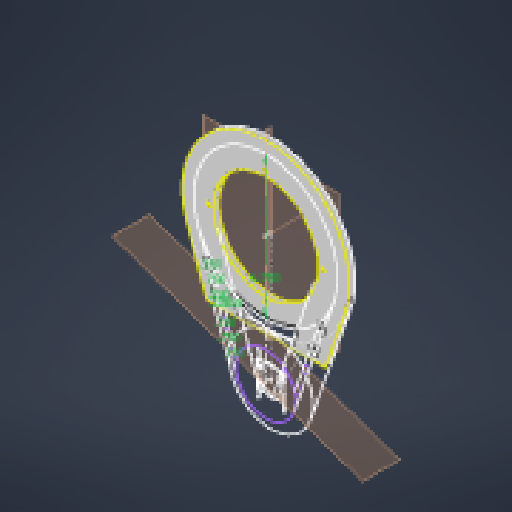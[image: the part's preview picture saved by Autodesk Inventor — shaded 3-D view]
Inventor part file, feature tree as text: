
AUTODESK INVENTOR PART (.ipt)
format: ipt  version: 2024 (Build 280153000, 153)  size: 336,384 bytes
history: native  units: in
note: dims shown in document units (in); Inventor stores cm internally (conversion verified against a paired STEP export)
features: other x7, plane x3, sketch x3, extrude x3, fillet x2, reference x2, mirror x1, hole x1, projected_geometry x1
ambient origin geometry x8: Origin, YZ Plane, XZ Plane, XY Plane, X Axis, Y Axis, Z Axis, Center Point
bodies: Solid1 (feature_tree)
feature tree (23):
  plane  "Work Plane1"
  sketch  "Sketch1"  dims[d0=0.9518in d1=6.0in]
  extrude  "Extrusion1"  Depth=6.0in
  sketch  "Sketch2"  dims[d2=0.25in d3=0.0in d4=7.874in d5=3.937in d6=1.22in]
  extrude  "Extrusion2"  Depth=3.937in
  fillet  "Fillet1"  Radius=3.937in
  fillet  "Fillet2"  Radius=1.22in
  plane  "Work Plane2"
  extrude  "Extrusion3"  Depth=0.35in
  plane  "Work Plane3"
  mirror  "Mirror1"
  hole  "Hole1"  [1 undecoded]
  reference  "Reference1"
  reference  "Reference3"
  projected_geometry  "Projected Loop1"
  sketch  "Sketch3"  dims[d7=1.22in d8=0.134in d9=0.75in d10=0.248in d11=0.25in d12=90.0deg d13=1.0in d14=0.8108in d15=0.35in d16=0.1181in d17=0.35in d18=0.1181in d19=0.35in d20=0.1181in d21=0.35in d22=0.1181in d23=0.25in d24=6.75in d26=1.0in d27=0.0in d28=0.0in d29=0.0625in d30=0.125in d32=0.25in d33=0.35in d34=0.75in d35=0.35in d36=0.35in d37=0.75in d38=0.35in d39=0.0625in d40=0.313in d41=0.0in d42=0.0in]
  other  "Work Axis1"
  other  "<userpath>\CodingProjects\C-AAM\CAD\V1\Base.iam"
  other  "Base.iam"
  other  "LazySusan:1"
  other  "OR:1"
  other  "LargePitchAssembly:1"
  other  "HTD-5-Master:1"
note: 1 required parameter value undecoded (feature->parameter linkage not recoverable at this tier; creation-order binding heuristic only, values carry confidence <= 0.55)
